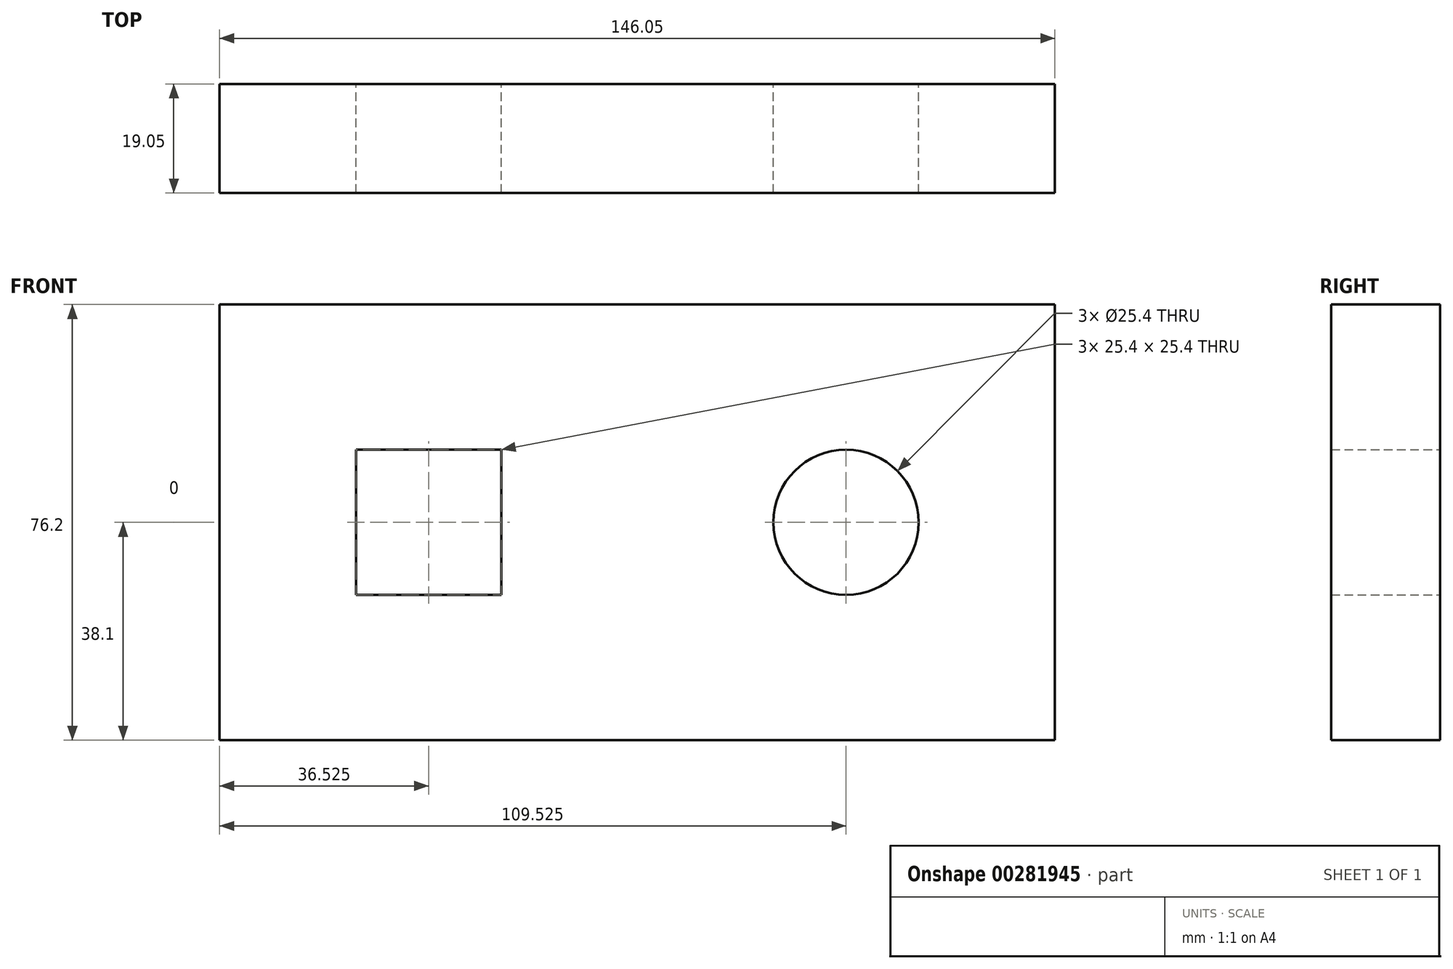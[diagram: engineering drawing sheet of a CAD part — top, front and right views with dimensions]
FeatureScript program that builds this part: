
annotation { "Feature Type Name" : "Feature", "Feature Type Description" : "" }
export const myFeature = defineFeature(function(context is Context, id is Id, definition is map)
    precondition{}
    {
        {
            var Q0;
            Q0=qCreatedBy(makeId("Front.planeOp"),FACE);
            var sketch = newSketch(context, id + "F0", { "sketchPlane" : qUnion([Q0])});
            skLineSegment(sketch, "E0.bottom", {"start": v(0, 0) * mm, "end": v(-146.05, 0) * mm});
            skLineSegment(sketch, "E0.top", {"start": v(0, 76.2) * mm, "end": v(-146.05, 76.2) * mm});
            skLineSegment(sketch, "E0.left", {"start": v(0, 0) * mm, "end": v(0, 76.2) * mm});
            skLineSegment(sketch, "E0.right", {"start": v(-146.05, 0) * mm, "end": v(-146.05, 76.2) * mm});
            skLineSegment(sketch, "E1.bottom", {"start": v(-122.22, 50.8) * mm, "end": v(-96.82, 50.8) * mm});
            skLineSegment(sketch, "E1.top", {"start": v(-122.22, 25.4) * mm, "end": v(-96.82, 25.4) * mm});
            skLineSegment(sketch, "E1.left", {"start": v(-122.22, 50.8) * mm, "end": v(-122.22, 25.4) * mm});
            skLineSegment(sketch, "E1.right", {"start": v(-96.82, 50.8) * mm, "end": v(-96.82, 25.4) * mm});
            skCircle(sketch, "E2", {"center": v(-36.53, 38.1) * mm, "radius": 12.7 * mm});
            skSolve(sketch);
        }
        {
            var Q0;
            Q0=makeQuery(id+"F0.imprint","IMPRINT",FACE,{"disambiguationData":[TD([[makeQuery(id+"F0.imprint","IMPRINT",EDGE,{"derivedFrom":sQuery(id+"F0.wireOp",EDGE,"E0.bottom")}),-1.0]])]});
            extrude(context, id + "F1", {"entities" : qUnion([Q0]), "depth" : 19.05 * mm});
        }
    });
